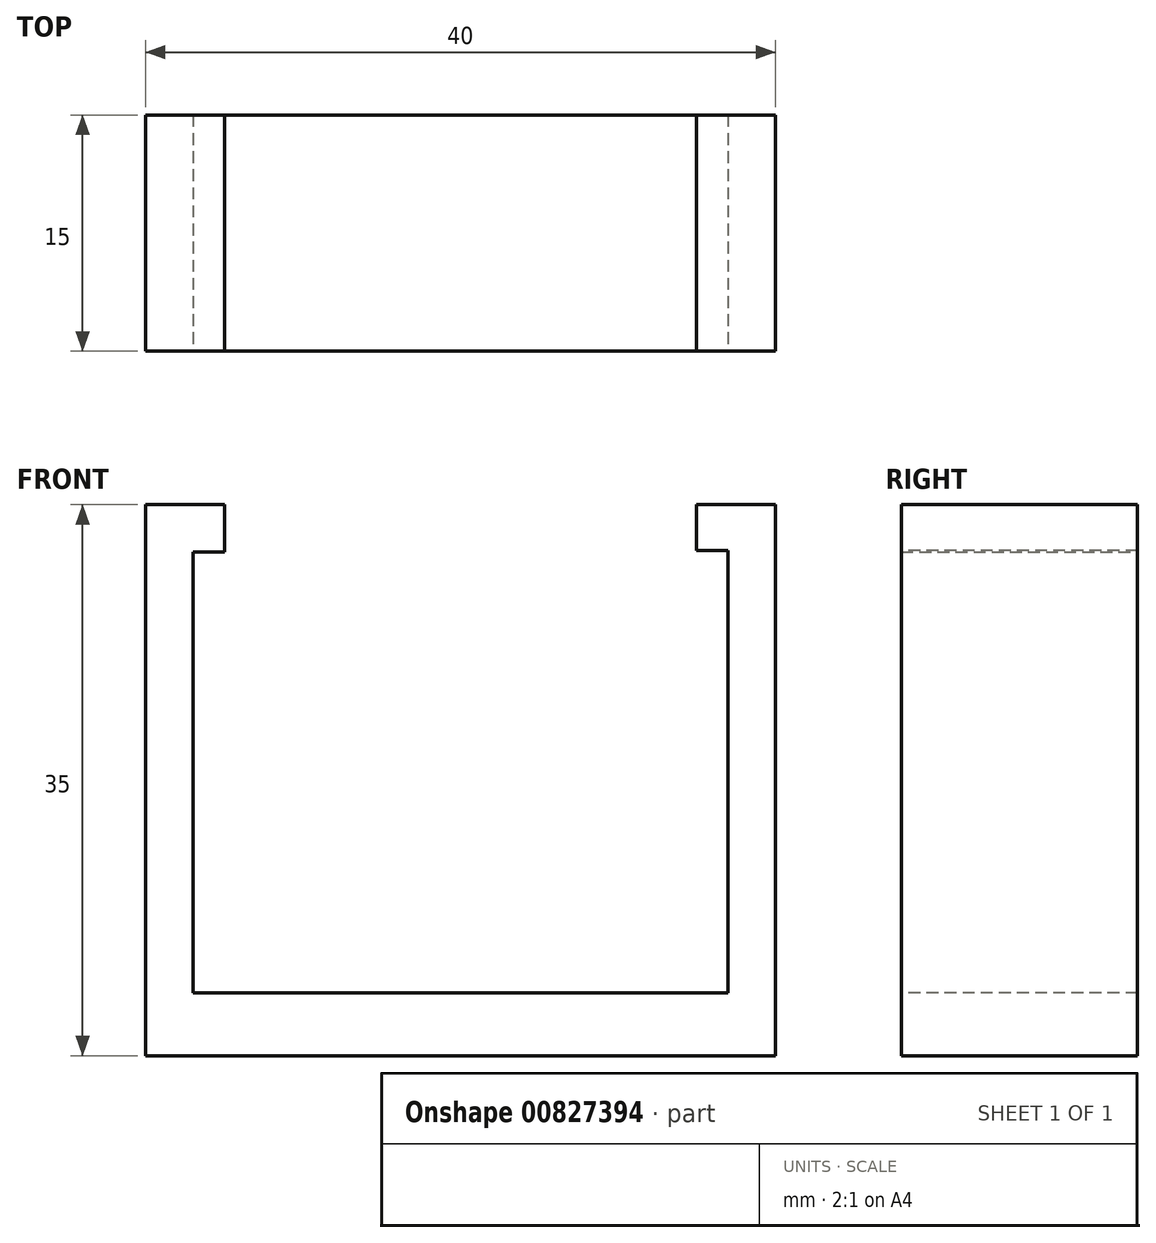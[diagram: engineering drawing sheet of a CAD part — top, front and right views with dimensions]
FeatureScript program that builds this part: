
annotation { "Feature Type Name" : "Feature", "Feature Type Description" : "" }
export const myFeature = defineFeature(function(context is Context, id is Id, definition is map)
    precondition{}
    {
        {
            var Q0;
            Q0=qCreatedBy(makeId("Top.planeOp"),FACE);
            var sketch = newSketch(context, id + "F0", { "sketchPlane" : qUnion([Q0])});
            skLineSegment(sketch, "E0.bottom", {"start": v(-44.92, 22.96) * mm, "end": v(-4.92, 22.96) * mm});
            skLineSegment(sketch, "E0.top", {"start": v(-44.92, 7.96) * mm, "end": v(-4.92, 7.96) * mm});
            skLineSegment(sketch, "E0.left", {"start": v(-44.92, 22.96) * mm, "end": v(-44.92, 7.96) * mm});
            skLineSegment(sketch, "E0.right", {"start": v(-4.92, 22.96) * mm, "end": v(-4.92, 7.96) * mm});
            skSolve(sketch);
        }
        {
            var Q0;
            Q0=makeQuery(id+"F0.imprint","IMPRINT",FACE,{"disambiguationData":[TD([[makeQuery(id+"F0.imprint","IMPRINT",EDGE,{"derivedFrom":sQuery(id+"F0.wireOp",EDGE,"E0.bottom")}),-1.0]])]});
            extrude(context, id + "F1", {"entities" : qUnion([Q0]), "depth" : 4 * mm, "offsetDistance" : 25 * mm});
        }
        {
            var Q0;
            Q0=makeQuery(id+"F1.opExtrude","CAP_FACE",FACE,{"disambiguationData":[OSD([sQuery(id+"F0.wireOp",EDGE,"E0.bottom"),sQuery(id+"F0.wireOp",EDGE,"E0.top"),sQuery(id+"F0.wireOp",EDGE,"E0.left"),sQuery(id+"F0.wireOp",EDGE,"E0.right")])],"isStart":false});
            var sketch = newSketch(context, id + "F2", { "sketchPlane" : qUnion([Q0])});
            skLineSegment(sketch, "E1.bottom", {"start": v(-44.92, 22.96) * mm, "end": v(-41.92, 22.96) * mm});
            skLineSegment(sketch, "E1.top", {"start": v(-44.92, 7.96) * mm, "end": v(-41.92, 7.96) * mm});
            skLineSegment(sketch, "E1.left", {"start": v(-44.92, 22.96) * mm, "end": v(-44.92, 7.96) * mm});
            skLineSegment(sketch, "E1.right", {"start": v(-41.92, 22.96) * mm, "end": v(-41.92, 7.96) * mm});
            skLineSegment(sketch, "E2.bottom", {"start": v(-7.92, 22.96) * mm, "end": v(-4.92, 22.96) * mm});
            skLineSegment(sketch, "E2.top", {"start": v(-7.92, 7.96) * mm, "end": v(-4.92, 7.96) * mm});
            skLineSegment(sketch, "E2.left", {"start": v(-7.92, 22.96) * mm, "end": v(-7.92, 7.96) * mm});
            skLineSegment(sketch, "E2.right", {"start": v(-4.92, 22.96) * mm, "end": v(-4.92, 7.96) * mm});
            skSolve(sketch);
        }
        {
            var Q0;
            Q0=makeQuery(id+"F2.imprint","IMPRINT",FACE,{"disambiguationData":[TD([[makeQuery(id+"F2.imprint","IMPRINT",EDGE,{"derivedFrom":sQuery(id+"F2.wireOp",EDGE,"E1.bottom")}),-1.0]])]});
            var Q1;
            Q1=makeQuery(id+"F2.imprint","IMPRINT",FACE,{"disambiguationData":[TD([[makeQuery(id+"F2.imprint","IMPRINT",EDGE,{"derivedFrom":sQuery(id+"F2.wireOp",EDGE,"E2.bottom")}),-1.0]])]});
            extrude(context, id + "F3", {"entities" : qUnion([Q0, Q1]), "operationType" : NewBodyOperationType.ADD, "depth" : 31 * mm, "offsetDistance" : 25 * mm});
        }
        {
            var Q0;
            Q0=makeQuery(id+"F3.opExtrude","SWEPT_FACE",FACE,{"disambiguationData":[OSD([sQuery(id+"F2.wireOp",EDGE,"E1.right")])]});
            var sketch = newSketch(context, id + "F4", { "sketchPlane" : qUnion([Q0])});
            skLineSegment(sketch, "E3.bottom", {"start": v(7.96, 35) * mm, "end": v(22.96, 35) * mm});
            skLineSegment(sketch, "E3.top", {"start": v(7.96, 32) * mm, "end": v(22.96, 32) * mm});
            skLineSegment(sketch, "E3.left", {"start": v(7.96, 35) * mm, "end": v(7.96, 32) * mm});
            skLineSegment(sketch, "E3.right", {"start": v(22.96, 35) * mm, "end": v(22.96, 32) * mm});
            skSolve(sketch);
        }
        {
            var Q0;
            Q0=makeQuery(id+"F4.imprint","IMPRINT",FACE,{"disambiguationData":[TD([[makeQuery(id+"F4.imprint","IMPRINT",EDGE,{"derivedFrom":sQuery(id+"F4.wireOp",EDGE,"E3.bottom")}),1.0]])]});
            extrude(context, id + "F5", {"entities" : qUnion([Q0]), "operationType" : NewBodyOperationType.ADD, "depth" : 2 * mm, "offsetDistance" : 25 * mm});
        }
        {
            var Q0;
            Q0=makeQuery(id+"F3.opExtrude","SWEPT_FACE",FACE,{"disambiguationData":[OSD([sQuery(id+"F2.wireOp",EDGE,"E2.left")])]});
            var sketch = newSketch(context, id + "F6", { "sketchPlane" : qUnion([Q0])});
            skLineSegment(sketch, "E4.bottom", {"start": v(-22.96, 35) * mm, "end": v(-7.96, 35) * mm});
            skLineSegment(sketch, "E4.top", {"start": v(-22.96, 32.1) * mm, "end": v(-7.96, 32.1) * mm});
            skLineSegment(sketch, "E4.left", {"start": v(-22.96, 35) * mm, "end": v(-22.96, 32.1) * mm});
            skLineSegment(sketch, "E4.right", {"start": v(-7.96, 35) * mm, "end": v(-7.96, 32.1) * mm});
            skSolve(sketch);
        }
        {
            var Q0;
            Q0=makeQuery(id+"F6.imprint","IMPRINT",FACE,{"disambiguationData":[TD([[makeQuery(id+"F6.imprint","IMPRINT",EDGE,{"derivedFrom":sQuery(id+"F6.wireOp",EDGE,"E4.bottom")}),-1.0]])]});
            extrude(context, id + "F7", {"entities" : qUnion([Q0]), "operationType" : NewBodyOperationType.ADD, "depth" : 2 * mm, "offsetDistance" : 25 * mm});
        }
    });
